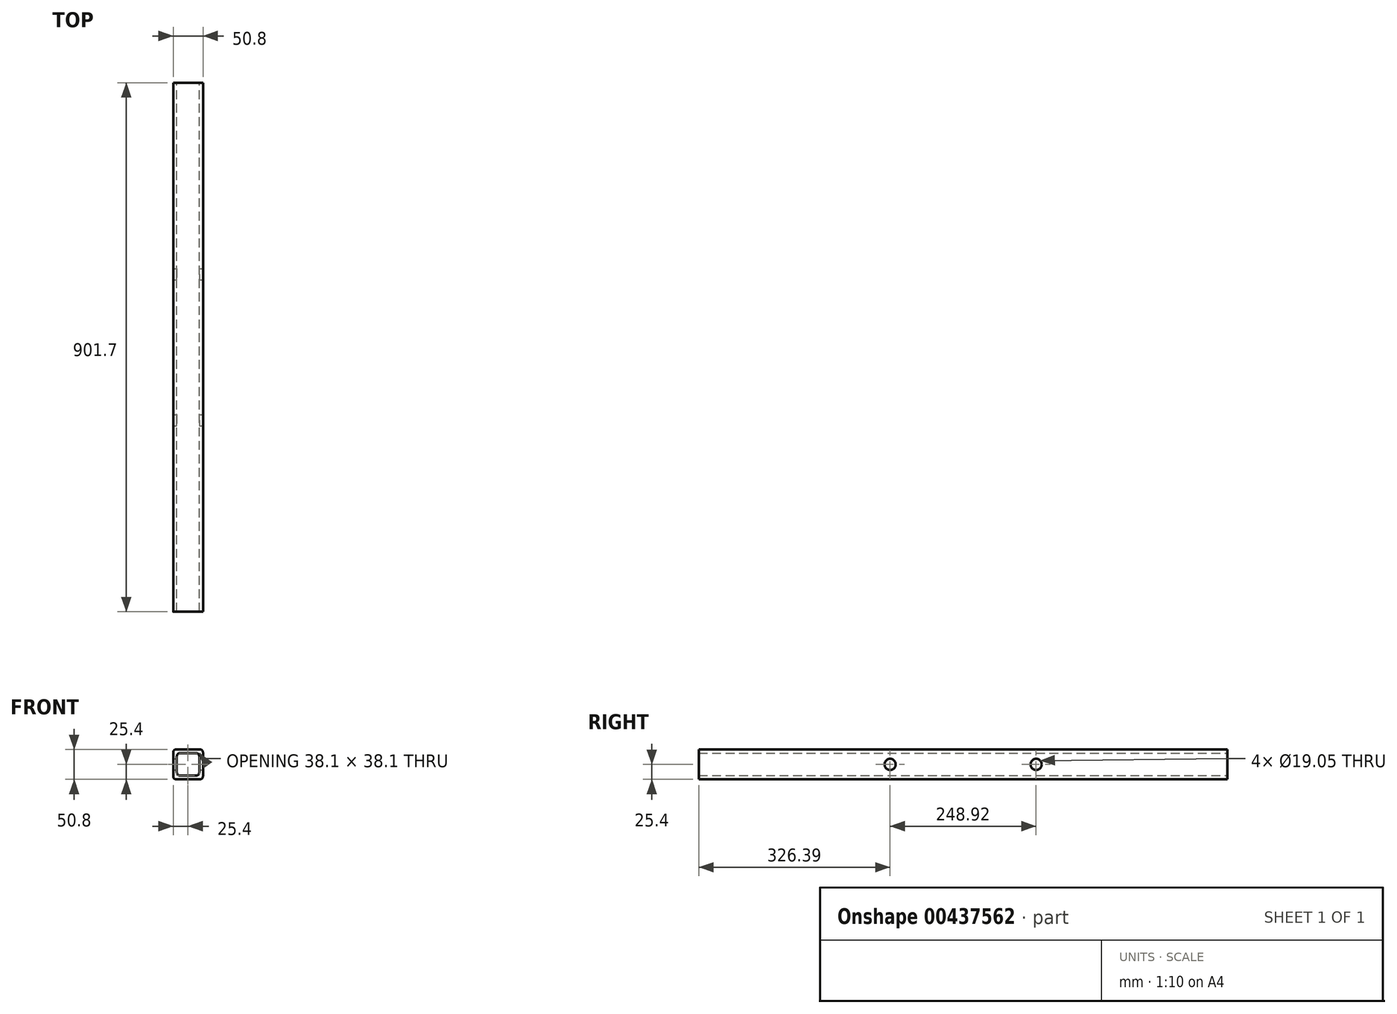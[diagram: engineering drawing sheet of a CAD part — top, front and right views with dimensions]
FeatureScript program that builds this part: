
annotation { "Feature Type Name" : "Feature", "Feature Type Description" : "" }
export const myFeature = defineFeature(function(context is Context, id is Id, definition is map)
    precondition{}
    {
        {
            var Q0;
            Q0=qCreatedBy(makeId("Front.planeOp"),FACE);
            var sketch = newSketch(context, id + "F0", { "sketchPlane" : qUnion([Q0])});
            skLineSegment(sketch, "E0.bottom", {"start": v(25.4, -25.4) * mm, "end": v(-25.4, -25.4) * mm});
            skLineSegment(sketch, "E0.top", {"start": v(25.4, 25.4) * mm, "end": v(-25.4, 25.4) * mm});
            skLineSegment(sketch, "E0.left", {"start": v(25.4, -25.4) * mm, "end": v(25.4, 25.4) * mm});
            skLineSegment(sketch, "E0.right", {"start": v(-25.4, -25.4) * mm, "end": v(-25.4, 25.4) * mm});
            skPoint(sketch, "E0.middle", {"position": v(0, 0) * mm});
            skLineSegment(sketch, "E1.bottom", {"start": v(19.05, -19.05) * mm, "end": v(-19.05, -19.05) * mm});
            skLineSegment(sketch, "E1.top", {"start": v(19.05, 19.05) * mm, "end": v(-19.05, 19.05) * mm});
            skLineSegment(sketch, "E1.left", {"start": v(19.05, -19.05) * mm, "end": v(19.05, 19.05) * mm});
            skLineSegment(sketch, "E1.right", {"start": v(-19.05, -19.05) * mm, "end": v(-19.05, 19.05) * mm});
            skSolve(sketch);
        }
        {
            var Q0;
            Q0 = qSketchRegion(id + "F0", true);
            extrude(context, id + "F1", {"entities" : qUnion([Q0]), "endBound" : BoundingType.SYMMETRIC, "depth" : 901.7 * mm});
        }
        {
            var Q0;
            Q0=makeQuery(id+"F1.opExtrude","SWEPT_FACE",FACE,{"disambiguationData":[OSD([sQuery(id+"F0.wireOp",EDGE,"E0.left")])]});
            var sketch = newSketch(context, id + "F2", { "sketchPlane" : qUnion([Q0])});
            skCircle(sketch, "E2", {"center": v(-124.46, 0) * mm, "radius": 9.53 * mm});
            skCircle(sketch, "E3.MirrorC", {"center": v(124.46, 0) * mm, "radius": 9.53 * mm});
            skSolve(sketch);
        }
        {
            var Q0;
            Q0 = qSketchRegion(id + "F2", true);
            extrude(context, id + "F3", {"entities" : qUnion([Q0]), "operationType" : NewBodyOperationType.REMOVE, "endBound" : BoundingType.THROUGH_ALL, "oppositeDirection" : true, "depth" : 50.8 * mm});
        }
        {
            var Q0;
            Q0=makeQuery(id+"F1.opExtrude","SWEPT_EDGE",EDGE,{"disambiguationData":[OSD([sQuery(id+"F0.wireOp",EDGE,"E0.top"),sQuery(id+"F0.wireOp",EDGE,"E0.right")])]});
            var Q1;
            Q1=makeQuery(id+"F1.opExtrude","SWEPT_EDGE",EDGE,{"disambiguationData":[OSD([sQuery(id+"F0.wireOp",EDGE,"E0.top"),sQuery(id+"F0.wireOp",EDGE,"E0.left")])]});
            var Q2;
            Q2=makeQuery(id+"F1.opExtrude","SWEPT_EDGE",EDGE,{"disambiguationData":[OSD([sQuery(id+"F0.wireOp",EDGE,"E1.bottom"),sQuery(id+"F0.wireOp",EDGE,"E1.left")])]});
            var Q3;
            Q3=makeQuery(id+"F1.opExtrude","SWEPT_EDGE",EDGE,{"disambiguationData":[OSD([sQuery(id+"F0.wireOp",EDGE,"E1.bottom"),sQuery(id+"F0.wireOp",EDGE,"E1.right")])]});
            var Q4;
            Q4=makeQuery(id+"F1.opExtrude","SWEPT_EDGE",EDGE,{"disambiguationData":[OSD([sQuery(id+"F0.wireOp",EDGE,"E0.bottom"),sQuery(id+"F0.wireOp",EDGE,"E0.right")])]});
            var Q5;
            Q5=makeQuery(id+"F1.opExtrude","SWEPT_EDGE",EDGE,{"disambiguationData":[OSD([sQuery(id+"F0.wireOp",EDGE,"E0.bottom"),sQuery(id+"F0.wireOp",EDGE,"E0.left")])]});
            var Q6;
            Q6=makeQuery(id+"F1.opExtrude","SWEPT_EDGE",EDGE,{"disambiguationData":[OSD([sQuery(id+"F0.wireOp",EDGE,"E1.top"),sQuery(id+"F0.wireOp",EDGE,"E1.left")])]});
            var Q7;
            Q7=makeQuery(id+"F1.opExtrude","SWEPT_EDGE",EDGE,{"disambiguationData":[OSD([sQuery(id+"F0.wireOp",EDGE,"E1.top"),sQuery(id+"F0.wireOp",EDGE,"E1.right")])]});
            fillet(context, id + "F4", {"entities" : qUnion([Q0, Q1, Q2, Q3, Q4, Q5, Q6, Q7]), "radius" : 5.08 * mm, "tangentPropagation" : true, "allowEdgeOverflow" : false});
        }
    });
